# Revit family: Soap_Dispenser-Sloan-ESD-2100
name_source: partatom
category: Specialty Equipment
revit_build: Autodesk Revit 2014 (Build: 20130308_1515(x64)
units: mm (PartAtom-declared; Revit-internal decimal feet)

## types (1)
- ESD-2100
    ADA Compliant = Yes
    Assembly Code = E1010900
    Code Number = 3346098
    Countertop Thickness = 1"
    Default Elevation = 0"
    Description = Sensor Activated Electronic Soap Dispenser
    Finish = Die Cast-Sloan-Chrome Plated
    Height = 3 31/32"
    Installation Type = Deck Mounted
    Length = 4 21/32"
    Manufacturer = SLOAN
    Material = Die Cast-Sloan-Chrome Plated
    Model = ESD-2100
    Operation = Sensor Activated
    Price = Prices may vary. Please consult Manufacturer Representative for most up-to-date price list.
    Product Documentation Link = https://specifications.sloan.com
    Product Page URL = https://www.sloan.com
    URL = https://www.sloan.com
    Voltage = 120 V
    Warranty Information = 3 Year Limited Warranty
    Width = 2 9/32"

## geometry (parser evidence)
native form markers: Sweep x1
no freeform markers — native parametric forms only
